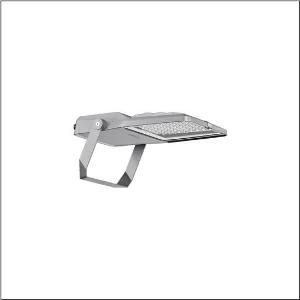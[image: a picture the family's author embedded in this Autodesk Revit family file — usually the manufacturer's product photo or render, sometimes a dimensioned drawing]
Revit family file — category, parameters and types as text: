
# Revit family: floodlight_fl_21_iq_mini___pl33t_5xa7771b2f1a_e875
name_source: partatom
category: Lighting Fixtures
units: mm (PartAtom-declared; Revit-internal decimal feet)

## family parameters
Cut with Voids When Loaded = No
Host = Face
Light Source = No
Part Type = Normal
Room Calculation Point = No
Round Connector Dimension = Use Diameter
Shared = No

## types (1)
- --- (1 x LED, 6170 lm, 45.5 W, 3000K)
    Apparent Load = 46 VA
    CIE Flux Codes = 26 75 99 100 100
    Color Rendering = 70
    Color Temperature = 3000K
    Default Elevation = 1800 mm
    Description = Floodlight FL 21 iQ mini, floodlight, primary light control with lens, of PMMA, primary optical cover: protective disc, of toughened safety glass, transparent, light distribution: PL33T, light emission: direct distribution, installation type: surface-mounted, LED, High Power LED, rated luminous flux: 6.170lm, luminous efficacy: 136lm/W, light colour: 730, colour temperature: 3000K, control: Auto-Match, Temp-Guard, Lumen-Switch, Night-Set, Smart-Wire, Light-Fading, Desk-Remote (wireless, voltage-free reading and setting of iQ features in the workshop via application-optimized NFC function/RFID function), optimised constant luminous flux control (CLO 2.0), with terminal, 6-pole, mains connection: 220..240V, AC, 50/60Hz, start of lifetime: 46W, end of service life: 48W, reduction: 22W, luminaire housing, of diecast aluminium, powder-coated, Siteco® metallic grey (DB 702S), corrosivity category C5 mid according to DIN EN ISO 12944, sealing non-destructively replaceable, mounting bracket, of steel, galvanised, powder-coated, Siteco® metallic grey (DB 702S), protection rating (complete): IP66, insulation class (complete): insulation class II (safety insulation), certification: CE, ENEC, VDE, protection symbol: D, impact resistance: IK08, permissible operating ambient temperature: -40..+40°C, permissible operating ambient temperature for outdoor applications: -40..+50°C, standard: DIN EN 12944, LABS conformity tested according to VDMA 24364:2018-05, packaging unit: 1 piece

Light Distribution: PL33T
    Height = 70 mm
    Lamp = 1 x LED
    Lamp Light Flux = 6170 lm
    Lamp Power = 45.5 W
    Lamp count = 1
    Length = 485 mm
    Luminous efficacy = 136 lm/W
    Manufacturer = Siteco
    ModVariant = No
    Model = 5XA7771B2F1A
    Mounting Place = Wall
    Mounting Type = Surface mounted
    Number of Poles = 1
    OnlyDefault = Yes
    Power Factor = 1
    Product Name = Floodlight FL 21 iQ mini | PL33T
    Product group = floodlight | wall mounted
    ProductGroupID = 2001
    Protection Class = Protection class II
    Protection Degree = IP 66
    RLX_Detail_Level = 1
    RLX_Emergency_Light_Flux = 0 lm
    RLX_Emergency_Type = 0
    RLX_Emergency_Type_DB = No
    RlxData = <blob elided: 95945 chars, md5=8eb82c42>
    Socket = socket
    Standby Power = 0 W
    System Light Flux = 6170 lm
    System Power = 46 W
    Type Comments = factory setting: luminous flux: 100 % | dim-lin: 254 | 463 mA
    Type Image = l_1006845.jpg
    URL = http://relux.com
    VarID = @adj_082839
    Voltage = 0 V
    Weight = 0.00 kg
    Width = 337 mm

## geometry (parser evidence)
native form markers: Blend x4, Sweep x10
no freeform markers — native parametric forms only
